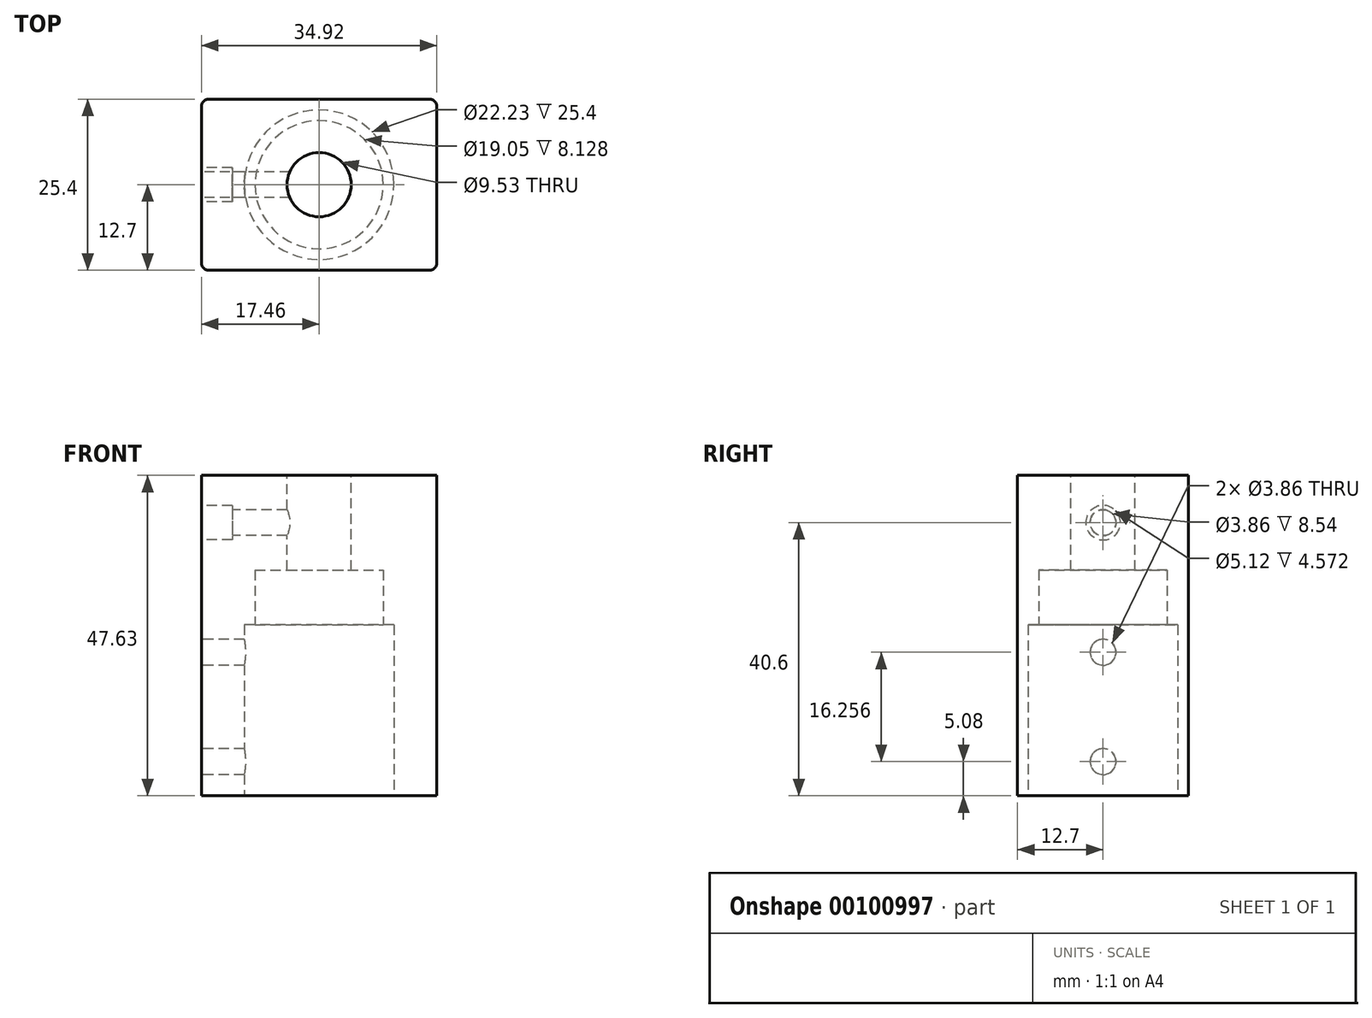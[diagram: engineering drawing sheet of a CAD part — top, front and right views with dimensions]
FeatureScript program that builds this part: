
annotation { "Feature Type Name" : "Feature", "Feature Type Description" : "" }
export const myFeature = defineFeature(function(context is Context, id is Id, definition is map)
    precondition{}
    {
        {
            var Q0;
            Q0=qCreatedBy(makeId("Top.planeOp"),FACE);
            var sketch = newSketch(context, id + "F0", { "sketchPlane" : qUnion([Q0])});
            skLineSegment(sketch, "E0.bottom", {"start": v(17.46, 12.7) * mm, "end": v(-17.46, 12.7) * mm});
            skLineSegment(sketch, "E0.top", {"start": v(17.46, -12.7) * mm, "end": v(-17.46, -12.7) * mm});
            skLineSegment(sketch, "E0.left", {"start": v(17.46, 12.7) * mm, "end": v(17.46, -12.7) * mm});
            skLineSegment(sketch, "E0.right", {"start": v(-17.46, 12.7) * mm, "end": v(-17.46, -12.7) * mm});
            skPoint(sketch, "E0.middle", {"position": v(0, 0) * mm});
            skSolve(sketch);
        }
        {
            var Q0;
            Q0 = qSketchRegion(id + "F0", true);
            extrude(context, id + "F1", {"entities" : qUnion([Q0]), "depth" : 47.62 * mm});
        }
        {
            var Q0;
            Q0=qCreatedBy(makeId("Top.planeOp"),FACE);
            var sketch = newSketch(context, id + "F2", { "sketchPlane" : qUnion([Q0])});
            skCircle(sketch, "E1", {"center": v(0, 0) * mm, "radius": 11.11 * mm});
            skSolve(sketch);
        }
        {
            var Q0;
            Q0 = qSketchRegion(id + "F2", true);
            extrude(context, id + "F3", {"entities" : qUnion([Q0]), "operationType" : NewBodyOperationType.REMOVE, "depth" : 25.4 * mm});
        }
        {
            var Q0;
            Q0=makeQuery(id+"F3.boolean.opBoolean","COPY",FACE,{"derivedFrom":makeQuery(id+"F3.opExtrude","CAP_FACE",FACE,{"disambiguationData":[OSD([sQuery(id+"F2.wireOp",EDGE,"E1")])],"isStart":false})});
            var sketch = newSketch(context, id + "F4", { "sketchPlane" : qUnion([Q0])});
            skCircle(sketch, "E2", {"center": v(0, 0) * mm, "radius": 9.53 * mm});
            skSolve(sketch);
        }
        {
            var Q0;
            Q0 = qSketchRegion(id + "F4", true);
            extrude(context, id + "F5", {"entities" : qUnion([Q0]), "operationType" : NewBodyOperationType.REMOVE, "oppositeDirection" : true, "depth" : 8.13 * mm});
        }
        {
            var Q0;
            Q0=makeQuery(id+"F1.opExtrude","CAP_FACE",FACE,{"disambiguationData":[OSD([sQuery(id+"F0.wireOp",EDGE,"E0.bottom"),sQuery(id+"F0.wireOp",EDGE,"E0.top"),sQuery(id+"F0.wireOp",EDGE,"E0.left"),sQuery(id+"F0.wireOp",EDGE,"E0.right")])],"isStart":false});
            var sketch = newSketch(context, id + "F6", { "sketchPlane" : qUnion([Q0])});
            skCircle(sketch, "E3", {"center": v(0, 0) * mm, "radius": 4.76 * mm});
            skSolve(sketch);
        }
        {
            var Q0;
            Q0 = qSketchRegion(id + "F6", true);
            extrude(context, id + "F7", {"entities" : qUnion([Q0]), "operationType" : NewBodyOperationType.REMOVE, "oppositeDirection" : true, "depth" : 25.4 * mm});
        }
        {
            var Q0;
            Q0=makeQuery(id+"F1.opExtrude","SWEPT_FACE",FACE,{"disambiguationData":[OSD([sQuery(id+"F0.wireOp",EDGE,"E0.right")])]});
            var sketch = newSketch(context, id + "F8", { "sketchPlane" : qUnion([Q0])});
            skCircle(sketch, "E4", {"center": v(0, 21.34) * mm, "radius": 1.93 * mm});
            skCircle(sketch, "E5", {"center": v(0, 5.08) * mm, "radius": 1.93 * mm});
            skCircle(sketch, "E6", {"center": v(0, 40.6) * mm, "radius": 1.93 * mm});
            skSolve(sketch);
        }
        {
            var Q0;
            Q0 = qSketchRegion(id + "F8", true);
            extrude(context, id + "F9", {"entities" : qUnion([Q0]), "operationType" : NewBodyOperationType.REMOVE, "oppositeDirection" : true, "depth" : 16.78 * mm});
        }
        {
            var Q0;
            Q0=makeQuery(id+"F1.opExtrude","SWEPT_EDGE",EDGE,{"disambiguationData":[OSD([sQuery(id+"F0.wireOp",EDGE,"E0.top"),sQuery(id+"F0.wireOp",EDGE,"E0.right")])]});
            var Q1;
            Q1=makeQuery(id+"F1.opExtrude","SWEPT_EDGE",EDGE,{"disambiguationData":[OSD([sQuery(id+"F0.wireOp",EDGE,"E0.top"),sQuery(id+"F0.wireOp",EDGE,"E0.left")])]});
            var Q2;
            Q2=makeQuery(id+"F1.opExtrude","SWEPT_EDGE",EDGE,{"disambiguationData":[OSD([sQuery(id+"F0.wireOp",EDGE,"E0.bottom"),sQuery(id+"F0.wireOp",EDGE,"E0.right")])]});
            var Q3;
            Q3=makeQuery(id+"F1.opExtrude","SWEPT_EDGE",EDGE,{"disambiguationData":[OSD([sQuery(id+"F0.wireOp",EDGE,"E0.bottom"),sQuery(id+"F0.wireOp",EDGE,"E0.left")])]});
            fillet(context, id + "F10", {"entities" : qUnion([Q0, Q1, Q2, Q3]), "radius" : 1.02 * mm, "tangentPropagation" : true, "allowEdgeOverflow" : false});
        }
        {
            var Q0;
            Q0=makeQuery(id+"F1.opExtrude","SWEPT_FACE",FACE,{"disambiguationData":[OSD([sQuery(id+"F0.wireOp",EDGE,"E0.right")])]});
            var sketch = newSketch(context, id + "F11", { "sketchPlane" : qUnion([Q0])});
            skCircle(sketch, "E7", {"center": v(0, 40.6) * mm, "radius": 2.56 * mm});
            skSolve(sketch);
        }
        {
            var Q0;
            Q0 = qSketchRegion(id + "F11", true);
            extrude(context, id + "F12", {"entities" : qUnion([Q0]), "operationType" : NewBodyOperationType.REMOVE, "oppositeDirection" : true, "depth" : 4.57 * mm});
        }
    });
